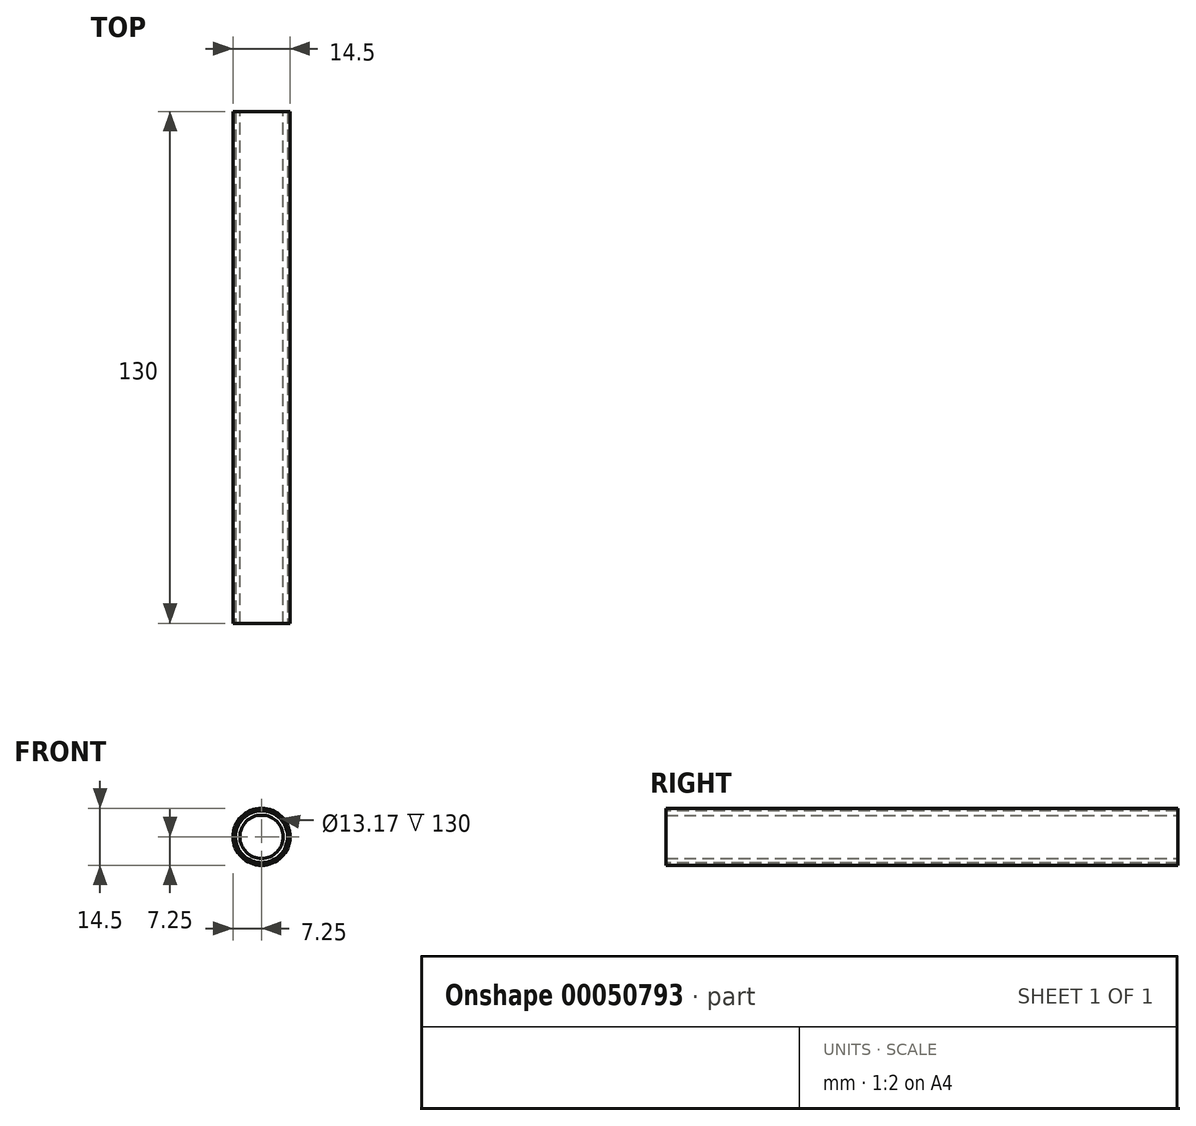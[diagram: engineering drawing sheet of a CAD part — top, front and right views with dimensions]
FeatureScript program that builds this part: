
annotation { "Feature Type Name" : "Feature", "Feature Type Description" : "" }
export const myFeature = defineFeature(function(context is Context, id is Id, definition is map)
    precondition{}
    {
        {
            var Q0;
            Q0=qCreatedBy(makeId("Front.planeOp"),FACE);
            var sketch = newSketch(context, id + "F0", { "sketchPlane" : qUnion([Q0])});
            skCircle(sketch, "E0", {"center": v(0, 0) * mm, "radius": 7.25 * mm});
            skSolve(sketch);
        }
        {
            var Q0;
            Q0=makeQuery(id+"F0.imprint","IMPRINT",FACE,{"disambiguationData":[TD([[makeQuery(id+"F0.imprint","IMPRINT",EDGE,{"derivedFrom":sQuery(id+"F0.wireOp",EDGE,"E0")}),1.0]])]});
            extrude(context, id + "F1", {"entities" : qUnion([Q0]), "depth" : 130 * mm});
        }
        {
            var Q0;
            Q0=makeQuery(id+"F1.opExtrude","CAP_FACE",FACE,{"disambiguationData":[OSD([sQuery(id+"F0.wireOp",EDGE,"E0")])],"isStart":false});
            var sketch = newSketch(context, id + "F2", { "sketchPlane" : qUnion([Q0])});
            skCircle(sketch, "E1", {"center": v(0, 0) * mm, "radius": 6.59 * mm});
            skSolve(sketch);
        }
        {
            var Q0;
            Q0=makeQuery(id+"F2.imprint","IMPRINT",FACE,{"disambiguationData":[TD([[makeQuery(id+"F2.imprint","IMPRINT",EDGE,{"derivedFrom":sQuery(id+"F2.wireOp",EDGE,"E1")}),1.0]])]});
            extrude(context, id + "F3", {"entities" : qUnion([Q0]), "operationType" : NewBodyOperationType.REMOVE, "oppositeDirection" : true, "depth" : 130 * mm});
        }
        {
            var Q0;
            Q0=qCreatedBy(makeId("Front.planeOp"),FACE);
            var sketch = newSketch(context, id + "F4", { "sketchPlane" : qUnion([Q0])});
            skCircle(sketch, "E2", {"center": v(0, 0) * mm, "radius": 5.5 * mm});
            skSolve(sketch);
        }
        {
            var Q0;
            Q0 = qSketchRegion(id + "F4", true);
            extrude(context, id + "F5", {"entities" : qUnion([Q0]), "depth" : 130 * mm});
        }
        {
            var Q0;
            Q0=makeQuery(id+"F5.opExtrude","CAP_FACE",FACE,{"disambiguationData":[OSD([sQuery(id+"F4.wireOp",EDGE,"E2")])],"isStart":false});
            var sketch = newSketch(context, id + "F6", { "sketchPlane" : qUnion([Q0])});
            skCircle(sketch, "E3", {"center": v(0, 0) * mm, "radius": 3.15 * mm});
            skSolve(sketch);
        }
        {
            var Q0;
            Q0 = qSketchRegion(id + "F6", true);
            extrude(context, id + "F7", {"entities" : qUnion([Q0]), "operationType" : NewBodyOperationType.ADD, "oppositeDirection" : true, "depth" : 130 * mm});
        }
    });
